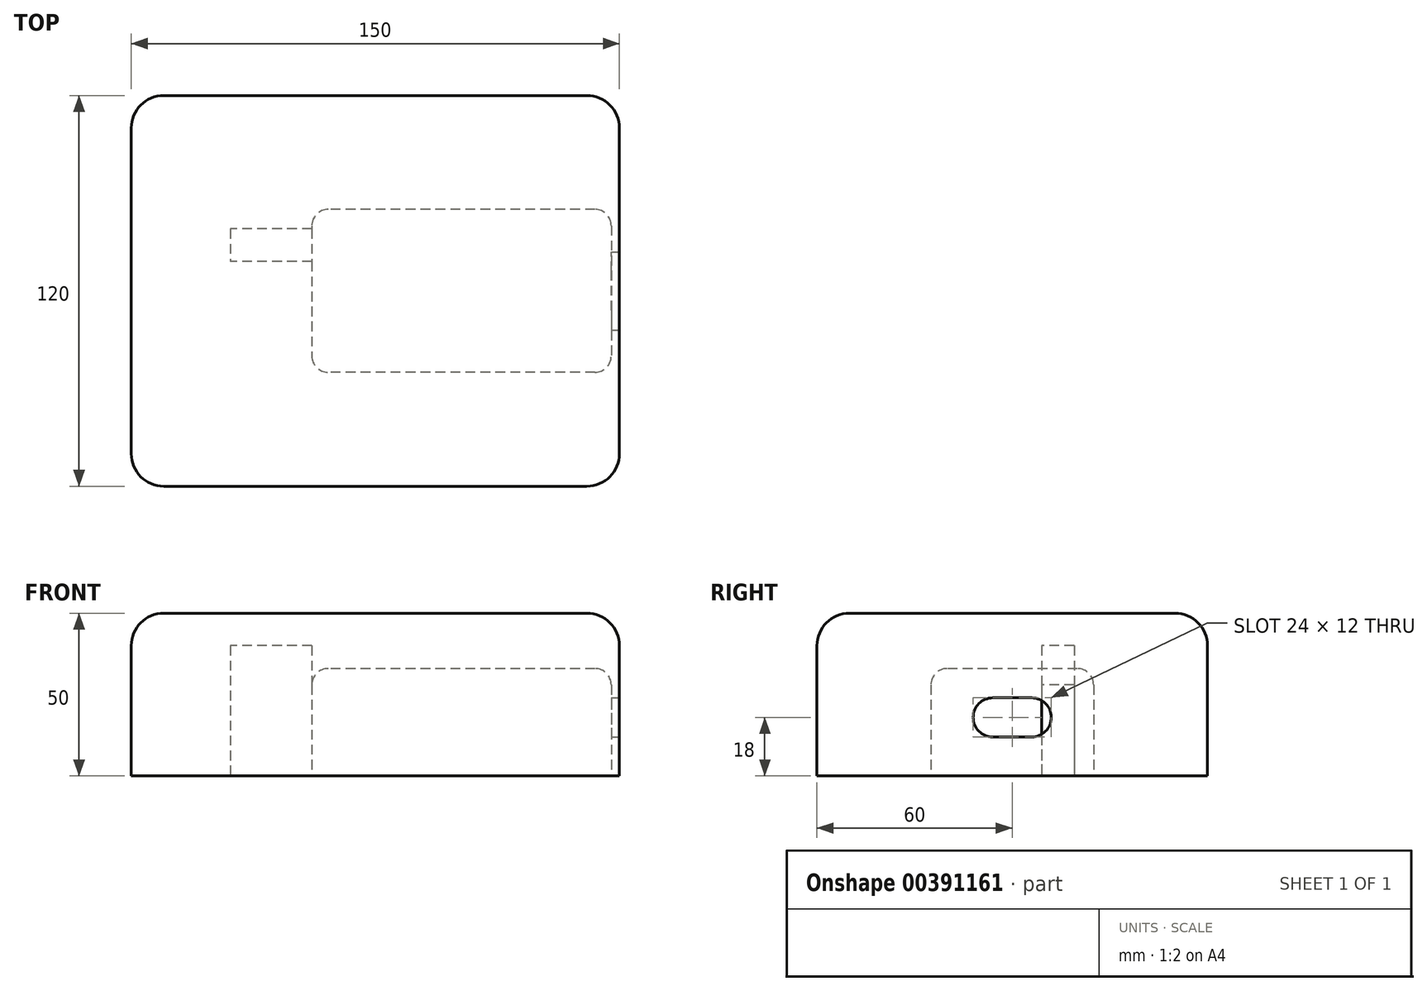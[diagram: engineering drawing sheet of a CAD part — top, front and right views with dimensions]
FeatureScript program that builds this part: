
annotation { "Feature Type Name" : "Feature", "Feature Type Description" : "" }
export const myFeature = defineFeature(function(context is Context, id is Id, definition is map)
    precondition{}
    {
        {
            var Q0;
            Q0=qCreatedBy(makeId("Top.planeOp"),FACE);
            var sketch = newSketch(context, id + "F0", { "sketchPlane" : qUnion([Q0])});
            skLineSegment(sketch, "E0.bottom", {"start": v(75, -60) * mm, "end": v(-75, -60) * mm});
            skLineSegment(sketch, "E0.top", {"start": v(75, 60) * mm, "end": v(-75, 60) * mm});
            skLineSegment(sketch, "E0.left", {"start": v(75, -60) * mm, "end": v(75, 60) * mm});
            skLineSegment(sketch, "E0.right", {"start": v(-75, -60) * mm, "end": v(-75, 60) * mm});
            skPoint(sketch, "E0.middle", {"position": v(0, 0) * mm});
            skSolve(sketch);
        }
        {
            var Q0;
            Q0 = qSketchRegion(id + "F0", true);
            extrude(context, id + "F1", {"entities" : qUnion([Q0]), "depth" : 50 * mm});
        }
        {
            var Q0;
            Q0=makeQuery(id+"F1.opExtrude","CAP_EDGE",EDGE,{"disambiguationData":[OSD([sQuery(id+"F0.wireOp",EDGE,"E0.bottom")])],"isStart":false});
            var Q1;
            Q1=makeQuery(id+"F1.opExtrude","CAP_EDGE",EDGE,{"disambiguationData":[OSD([sQuery(id+"F0.wireOp",EDGE,"E0.right")])],"isStart":false});
            var Q2;
            Q2=makeQuery(id+"F1.opExtrude","CAP_EDGE",EDGE,{"disambiguationData":[OSD([sQuery(id+"F0.wireOp",EDGE,"E0.top")])],"isStart":false});
            var Q3;
            Q3=makeQuery(id+"F1.opExtrude","CAP_EDGE",EDGE,{"disambiguationData":[OSD([sQuery(id+"F0.wireOp",EDGE,"E0.left")])],"isStart":false});
            var Q4;
            Q4=makeQuery(id+"F1.opExtrude","SWEPT_EDGE",EDGE,{"disambiguationData":[OSD([sQuery(id+"F0.wireOp",EDGE,"E0.bottom"),sQuery(id+"F0.wireOp",EDGE,"E0.right")])]});
            var Q5;
            Q5=makeQuery(id+"F1.opExtrude","SWEPT_EDGE",EDGE,{"disambiguationData":[OSD([sQuery(id+"F0.wireOp",EDGE,"E0.bottom"),sQuery(id+"F0.wireOp",EDGE,"E0.left")])]});
            var Q6;
            Q6=makeQuery(id+"F1.opExtrude","SWEPT_EDGE",EDGE,{"disambiguationData":[OSD([sQuery(id+"F0.wireOp",EDGE,"E0.top"),sQuery(id+"F0.wireOp",EDGE,"E0.left")])]});
            var Q7;
            Q7=makeQuery(id+"F1.opExtrude","SWEPT_EDGE",EDGE,{"disambiguationData":[OSD([sQuery(id+"F0.wireOp",EDGE,"E0.top"),sQuery(id+"F0.wireOp",EDGE,"E0.right")])]});
            fillet(context, id + "F2", {"entities" : qUnion([Q0, Q1, Q2, Q3, Q4, Q5, Q6, Q7]), "radius" : 10 * mm, "tangentPropagation" : true, "allowEdgeOverflow" : false});
        }
        {
            var Q0;
            Q0=makeQuery(id+"F1.opExtrude","CAP_FACE",FACE,{"disambiguationData":[OSD([sQuery(id+"F0.wireOp",EDGE,"E0.bottom"),sQuery(id+"F0.wireOp",EDGE,"E0.top"),sQuery(id+"F0.wireOp",EDGE,"E0.left"),sQuery(id+"F0.wireOp",EDGE,"E0.right")])],"isStart":true});
            var sketch = newSketch(context, id + "F3", { "sketchPlane" : qUnion([Q0])});
            skLineSegment(sketch, "E1", {"start": v(-58.98, 0) * mm, "end": v(84.28, 0) * mm, "construction": true});
            skPoint(sketch, "E1.endSnap0", {"position": v(75, 0) * mm});
            skLineSegment(sketch, "E2", {"start": v(26.5, 56.65) * mm, "end": v(26.5, -63.66) * mm, "construction": true});
            skLineSegment(sketch, "E3.bottom", {"start": v(72.5, -25) * mm, "end": v(-19.5, -25) * mm});
            skLineSegment(sketch, "E3.top", {"start": v(72.5, 25) * mm, "end": v(-19.5, 25) * mm});
            skLineSegment(sketch, "E3.left", {"start": v(72.5, -25) * mm, "end": v(72.5, 25) * mm});
            skLineSegment(sketch, "E3.right", {"start": v(-19.5, -25) * mm, "end": v(-19.5, 25) * mm});
            skPoint(sketch, "E3.middle", {"position": v(26.5, 0) * mm});
            skLineSegment(sketch, "E4", {"start": v(75, -61.96) * mm, "end": v(75, 63.87) * mm, "construction": true});
            skSolve(sketch);
        }
        {
            var Q0;
            Q0 = qSketchRegion(id + "F3", true);
            extrude(context, id + "F4", {"entities" : qUnion([Q0]), "operationType" : NewBodyOperationType.REMOVE, "oppositeDirection" : true, "depth" : 33 * mm});
        }
        {
            var Q0;
            Q0=makeQuery(id+"F4.boolean.opBoolean","COPY",FACE,{"derivedFrom":makeQuery(id+"F4.opExtrude","CAP_FACE",FACE,{"disambiguationData":[OSD([sQuery(id+"F3.wireOp",EDGE,"E3.bottom"),sQuery(id+"F3.wireOp",EDGE,"E3.top"),sQuery(id+"F3.wireOp",EDGE,"E3.left"),sQuery(id+"F3.wireOp",EDGE,"E3.right")])],"isStart":false})});
            var Q1;
            Q1=makeQuery(id+"F4.boolean.opBoolean","COPY",EDGE,{"derivedFrom":makeQuery(id+"F4.opExtrude","SWEPT_EDGE",EDGE,{"disambiguationData":[OSD([sQuery(id+"F3.wireOp",EDGE,"E3.top"),sQuery(id+"F3.wireOp",EDGE,"E3.right")])]})});
            var Q2;
            Q2=makeQuery(id+"F4.boolean.opBoolean","COPY",EDGE,{"derivedFrom":makeQuery(id+"F4.opExtrude","SWEPT_EDGE",EDGE,{"disambiguationData":[OSD([sQuery(id+"F3.wireOp",EDGE,"E3.top"),sQuery(id+"F3.wireOp",EDGE,"E3.left")])]})});
            var Q3;
            Q3=makeQuery(id+"F4.boolean.opBoolean","COPY",EDGE,{"derivedFrom":makeQuery(id+"F4.opExtrude","SWEPT_EDGE",EDGE,{"disambiguationData":[OSD([sQuery(id+"F3.wireOp",EDGE,"E3.bottom"),sQuery(id+"F3.wireOp",EDGE,"E3.right")])]})});
            var Q4;
            Q4=makeQuery(id+"F4.boolean.opBoolean","COPY",EDGE,{"derivedFrom":makeQuery(id+"F4.opExtrude","SWEPT_EDGE",EDGE,{"disambiguationData":[OSD([sQuery(id+"F3.wireOp",EDGE,"E3.bottom"),sQuery(id+"F3.wireOp",EDGE,"E3.left")])]})});
            fillet(context, id + "F5", {"entities" : qUnion([Q0, Q1, Q2, Q3, Q4]), "radius" : 5 * mm, "tangentPropagation" : true, "allowEdgeOverflow" : false});
        }
        {
            var Q0;
            Q0=makeQuery(id+"F1.opExtrude","CAP_FACE",FACE,{"disambiguationData":[OSD([sQuery(id+"F0.wireOp",EDGE,"E0.bottom"),sQuery(id+"F0.wireOp",EDGE,"E0.top"),sQuery(id+"F0.wireOp",EDGE,"E0.left"),sQuery(id+"F0.wireOp",EDGE,"E0.right")])],"isStart":true});
            var sketch = newSketch(context, id + "F6", { "sketchPlane" : qUnion([Q0])});
            skLineSegment(sketch, "E5", {"start": v(-60.36, -14) * mm, "end": v(20.92, -14) * mm, "construction": true});
            skLineSegment(sketch, "E6.bottom", {"start": v(-14.5, -19.02) * mm, "end": v(-44.5, -19.02) * mm});
            skLineSegment(sketch, "E6.top", {"start": v(-14.5, -8.98) * mm, "end": v(-44.5, -8.98) * mm});
            skLineSegment(sketch, "E6.left", {"start": v(-14.5, -19.02) * mm, "end": v(-14.5, -8.98) * mm});
            skLineSegment(sketch, "E6.right", {"start": v(-44.5, -19.02) * mm, "end": v(-44.5, -8.98) * mm});
            skPoint(sketch, "E6.middle", {"position": v(-29.5, -14) * mm});
            skLineSegment(sketch, "E7", {"start": v(-44.5, -8.98) * mm, "end": v(-44.5, 22.64) * mm, "construction": true});
            skSolve(sketch);
        }
        {
            var Q0;
            {var subQ0=sQuery(id+"F6.wireOp",EDGE,"E6.right");Q0=makeQuery(id+"F6.imprint","IMPRINT",FACE,{"disambiguationData":[TD([[makeQuery(id+"F6.imprint","IMPRINT",EDGE,{"derivedFrom":subQ0}),-1.0]])]});}
            extrude(context, id + "F7", {"entities" : qUnion([Q0]), "operationType" : NewBodyOperationType.REMOVE, "oppositeDirection" : true, "depth" : 40 * mm});
        }
        {
            var Q0;
            Q0=makeQuery(id+"F1.opExtrude","SWEPT_FACE",FACE,{"disambiguationData":[OSD([sQuery(id+"F0.wireOp",EDGE,"E0.left")])]});
            var sketch = newSketch(context, id + "F8", { "sketchPlane" : qUnion([Q0])});
            skLineSegment(sketch, "E8", {"start": v(0, 64.87) * mm, "end": v(0, -20.04) * mm, "construction": true});
            skPoint(sketch, "E9.first.point", {"position": v(0, 18) * mm});
            skPoint(sketch, "E9.second.point", {"position": v(-19.57, 18) * mm});
            skPoint(sketch, "E9.third.point", {"position": v(-14.5, 10.3) * mm});
            skLineSegment(sketch, "E10", {"start": v(-19.57, 18) * mm, "end": v(14, 18) * mm});
            skLineSegment(sketch, "E11", {"start": v(-6, 27.22) * mm, "end": v(-6, 1.82) * mm, "construction": true});
            skCircle(sketch, "E12", {"center": v(-6, 18) * mm, "radius": 6 * mm});
            skCircle(sketch, "E13.MirrorC", {"center": v(6, 18) * mm, "radius": 6 * mm});
            skLineSegment(sketch, "E14", {"start": v(-6, 24) * mm, "end": v(6, 24) * mm});
            skLineSegment(sketch, "E15", {"start": v(-6, 12) * mm, "end": v(6, 12) * mm});
            skSolve(sketch);
        }
        {
            var Q0;
            {var subQ0=sQuery(id+"F8.wireOp",EDGE,"E12");var subQ1=sQuery(id+"F8.wireOp",EDGE,"E10");var subQ2=makeQuery(id+"F8.imprint","INTERSECT",VERTEX,{"disambiguationData":[OD(0.0)],"derivedFrom":[subQ1,subQ0]});Q0=makeQuery(id+"F8.imprint","IMPRINT",FACE,{"disambiguationData":[TD([[makeQuery(id+"F8.imprint","IMPRINT",EDGE,{"disambiguationData":[TD([[subQ2,-1.0]])],"derivedFrom":subQ1}),-1.0]])]});}
            var Q1;
            {var subQ0=sQuery(id+"F8.wireOp",EDGE,"E12");var subQ1=sQuery(id+"F8.wireOp",EDGE,"E10");var subQ2=makeQuery(id+"F8.imprint","INTERSECT",VERTEX,{"disambiguationData":[OD(0.0)],"derivedFrom":[subQ1,subQ0]});Q1=makeQuery(id+"F8.imprint","IMPRINT",FACE,{"disambiguationData":[TD([[makeQuery(id+"F8.imprint","IMPRINT",EDGE,{"disambiguationData":[TD([[subQ2,-1.0]])],"derivedFrom":subQ1}),1.0]])]});}
            var Q2;
            {var subQ5=sQuery(id+"F8.wireOp",EDGE,"E14");Q2=makeQuery(id+"F8.imprint","IMPRINT",FACE,{"disambiguationData":[TD([[makeQuery(id+"F8.imprint","IMPRINT",EDGE,{"derivedFrom":subQ5}),-1.0]])]});}
            var Q3;
            {var subQ0=sQuery(id+"F8.wireOp",EDGE,"E13.MirrorC");var subQ1=sQuery(id+"F8.wireOp",EDGE,"E10");var subQ2=makeQuery(id+"F8.imprint","INTERSECT",VERTEX,{"disambiguationData":[OD(0.0)],"derivedFrom":[subQ1,subQ0]});Q3=makeQuery(id+"F8.imprint","IMPRINT",FACE,{"disambiguationData":[TD([[makeQuery(id+"F8.imprint","IMPRINT",EDGE,{"disambiguationData":[TD([[subQ2,1.0]])],"derivedFrom":subQ1}),1.0]])]});}
            var Q4;
            {var subQ0=sQuery(id+"F8.wireOp",EDGE,"E13.MirrorC");var subQ1=sQuery(id+"F8.wireOp",EDGE,"E10");var subQ2=makeQuery(id+"F8.imprint","INTERSECT",VERTEX,{"disambiguationData":[OD(0.0)],"derivedFrom":[subQ1,subQ0]});Q4=makeQuery(id+"F8.imprint","IMPRINT",FACE,{"disambiguationData":[TD([[makeQuery(id+"F8.imprint","IMPRINT",EDGE,{"disambiguationData":[TD([[subQ2,1.0]])],"derivedFrom":subQ1}),-1.0]])]});}
            var Q5;
            {var subQ5=sQuery(id+"F8.wireOp",EDGE,"E15");Q5=makeQuery(id+"F8.imprint","IMPRINT",FACE,{"disambiguationData":[TD([[makeQuery(id+"F8.imprint","IMPRINT",EDGE,{"derivedFrom":subQ5}),1.0]])]});}
            extrude(context, id + "F9", {"entities" : qUnion([Q0, Q1, Q2, Q3, Q4, Q5]), "operationType" : NewBodyOperationType.REMOVE, "oppositeDirection" : true, "depth" : 25 * mm});
        }
    });
